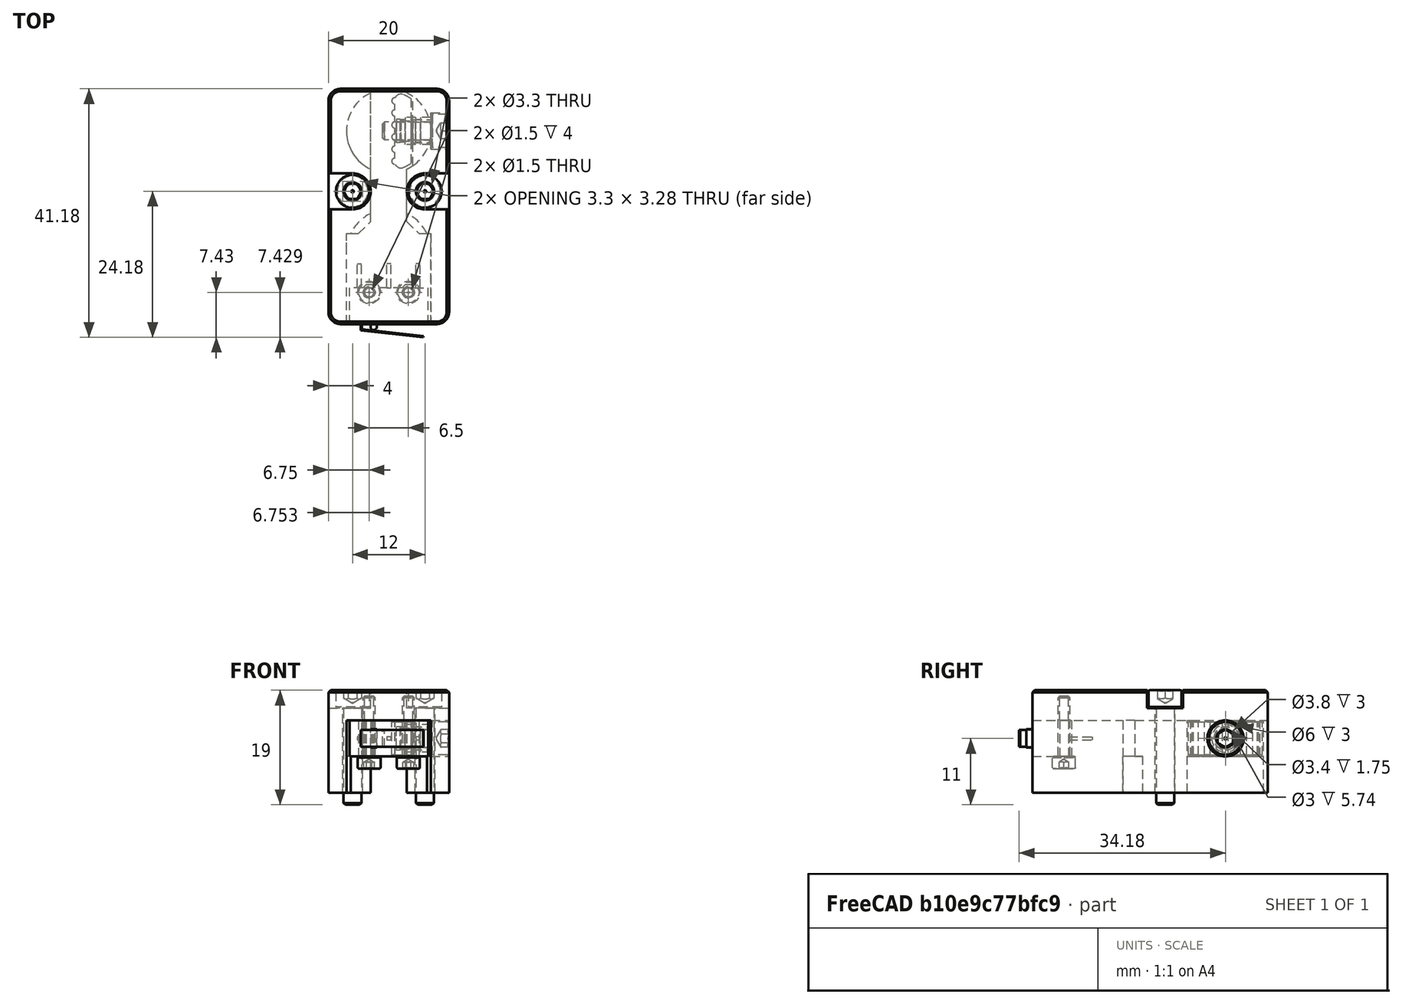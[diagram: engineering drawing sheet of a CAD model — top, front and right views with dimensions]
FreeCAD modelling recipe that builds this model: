
FCSTD DOCUMENT  (FreeCAD 0.19R24291 (Git))
Label: y-endstop-assembly
License: Other
LicenseURL: GPL3
objects: Part::FeaturePython×6, Part::Feature×3, PartDesign::CoordinateSystem×1, App::Part×1
note: 10 computed .brp shape members not serialized (recipe doc carries the construction recipe); baked Part::Feature solids carry a one-line shape summary decoded from their .brp

FEATURE [Part::Feature] Cut002008023012009006003002006002006002004004001  label="y-endstop-housing"
  shape: bbox 20 x 39 x 17 mm, 57 faces (baked)
FEATURE [Part::Feature] Fusion001001001011002001  label="y-endstop-wire-clamp"
  shape: bbox 3.25 x 12.25 x 5.5 mm, 20 faces (baked)
FEATURE [Part::Feature] Fusion001001001011002002  label="endstop-switch"
  Placement = pos=(0,0,6) rot=(0,0,1;0rad)
  shape: bbox 13 x 12.18 x 6 mm, 43 faces (baked)
FEATURE [Part::FeaturePython] HeatSet  label="M3x3-HeatSet"  # WARN: FeaturePython — macro-defined, semantics opaque (R4)
  Placement = pos=(7,32,9) rot=(0,1,0;1.5708rad)
  baseObject = -> Cut002008023012009006003002006002006002004004001 [Edge9]
  diameter = 2
  invert = false
  offset = 0
FEATURE [Part::FeaturePython] Screw  label="M3x16-Screw"  # Fasteners workbench fastener (typed FeaturePython)
  Placement = pos=(-6,22,14) rot=(0,0,1;0rad)
  baseObject = -> Cut002008023012009006003002006002006002004004001 [Edge109]
  diameter = 4
  invert = false
  length = 6
  lengthCustom = 16
  matchOuter = true
  offset = 0
  thread = false
  type = 34
FEATURE [Part::FeaturePython] Screw001  label="M3x16-Screw001"  # Fasteners workbench fastener (typed FeaturePython)
  Placement = pos=(6,22,14) rot=(0,0,1;0rad)
  baseObject = -> Cut002008023012009006003002006002006002004004001 [Edge133]
  diameter = 4
  invert = false
  length = 6
  lengthCustom = 16
  matchOuter = true
  offset = 0
  thread = false
  type = 34
FEATURE [PartDesign::CoordinateSystem] LCS_y_endstop  label="LCS_y-endstop"
  AttacherType = Attacher::AttachEngine3D
FEATURE [Part::FeaturePython] Screw003  label="M3x8-Screw"  # Fasteners workbench fastener (typed FeaturePython)
  Placement = pos=(7,32,9) rot=(0,1,0;1.5708rad)
  baseObject = -> HeatSet [Edge1]
  diameter = 4
  invert = false
  length = 2
  lengthCustom = 8
  matchOuter = true
  offset = 0
  thread = false
  type = 34
FEATURE [Part::FeaturePython] Screw004  label="M2x10-self-tapping001"  # Fasteners workbench fastener (typed FeaturePython)
  Placement = pos=(3.25262,5.24944,6.00292) rot=(3e-06,1,0;3.14159rad)
  baseObject = -> Fusion001001001011002002 [Edge107]
  diameter = 2
  invert = true
  length = 5
  lengthCustom = 10
  matchOuter = true
  offset = 0
  thread = false
  type = 34
FEATURE [Part::FeaturePython] Screw005  label="M2x10-self-tapping"  # Fasteners workbench fastener (typed FeaturePython)
  Placement = pos=(-3.24738,5.24944,6.00292) rot=(3e-06,1,0;3.14159rad)
  baseObject = -> Fusion001001001011002002 [Edge105]
  diameter = 2
  invert = true
  length = 5
  lengthCustom = 10
  matchOuter = true
  offset = 0
  thread = false
  type = 34
FEATURE [App::Part] Part  label="y-endstop"
  Group = -> [Cut002008023012009006003002006002006002004004001,Fusion001001001011002001,Fusion001001001011002002,HeatSet,Screw,Screw001,LCS_y_endstop,Screw003,Screw005,Screw004]
  Origin = -> Origin
